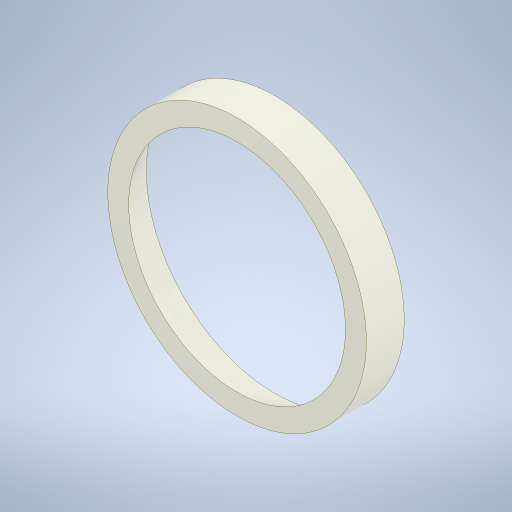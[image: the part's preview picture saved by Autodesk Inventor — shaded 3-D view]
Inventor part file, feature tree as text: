
AUTODESK INVENTOR PART (.ipt)
format: ipt  version: 2023.1 (Build 271208000, 208)  size: 242,176 bytes
history: native  units: mm
features: revolve x1, sketch x1
ambient origin geometry x8: Origin, YZ Plane, XZ Plane, XY Plane, X Axis, Y Axis, Z Axis, Center Point
bodies: Solid1 (feature_tree)
feature tree (2):
  revolve  "Revolution1"  [1 undecoded]
  sketch  "Sketch1"  dims[d0=4.886922mm d2=71.65mm d3=90.0deg d4=0.4mm d5=21.0mm]
note: 1 required parameter value undecoded (feature->parameter linkage not recoverable at this tier; creation-order binding heuristic only, values carry confidence <= 0.55)
